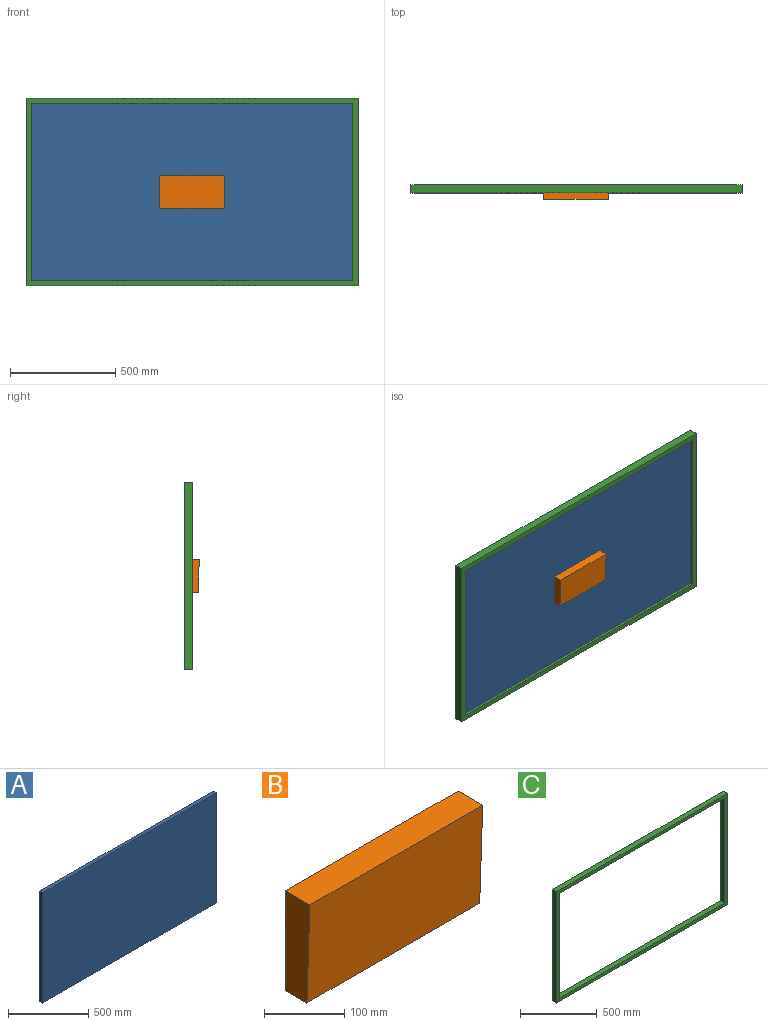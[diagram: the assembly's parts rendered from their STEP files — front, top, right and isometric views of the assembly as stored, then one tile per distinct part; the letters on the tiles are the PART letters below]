
ASSEMBLY  parts=3 mates=2
PART A: 6 faces, bbox 1524x25.4x838.2 mm
  f0: plane 1524x25.4mm, normal (0,0,1), area 38709.6mm2, adj f1,f3,f4,f5
  f1: plane 838.2x25.4mm, normal (-1,0,0), area 21290.3mm2, adj f0,f2,f4,f5
  f2: plane 1524x25.4mm, normal (0,0,-1), area 38709.6mm2, adj f1,f3,f4,f5
  f3: plane 838.2x25.4mm, normal (1,0,0), area 21290.3mm2, adj f0,f2,f4,f5
  f4: plane 1524x838.2mm, normal (0,-1,0), area 1277416.8mm2, adj f0,f1,f2,f3
  f5: plane 1524x838.2mm, normal (0,1,0), area 1277416.8mm2, adj f0,f1,f2,f3
PART B: 6 faces, bbox 304.8x43.4x152.4 mm
  f0: plane 304.8x152.4mm, normal (0,1,0), area 46451.5mm2, adj f1,f3,f4,f5
  f1: plane 304.8x43.42mm, normal (0,0,1), area 13235mm2, adj f0,f2,f4,f5
  f2: plane 304.8x152.4mm, normal (0,-1,-0.03), area 46479.8mm2, adj f1,f3,f4,f5
  f3: plane 304.8x38.1mm, normal (0,0,-1), area 11612.9mm2, adj f0,f2,f4,f5
  f4: plane 152.4x43.42mm, normal (1,0,0), area 6212mm2, adj f0,f1,f2,f3
  f5: plane 152.4x43.42mm, normal (-1,0,0), area 6212mm2, adj f0,f1,f2,f3
PART C: 10 faces, bbox 1574.8x38.1x889 mm
  f0: plane 1574.8x38.1mm, normal (0,0,1), area 59999.9mm2, adj f1,f7,f8,f9
  f1: plane 889x38.1mm, normal (-1,0,0), area 33870.9mm2, adj f0,f2,f8,f9
  f2: plane 1574.8x38.1mm, normal (0,0,-1), area 59999.9mm2, adj f1,f7,f8,f9
  f3: plane 838.2x38.1mm, normal (1,0,0), area 31935.4mm2, adj f4,f6,f8,f9
  f4: plane 1524x38.1mm, normal (0,0,-1), area 58064.4mm2, adj f3,f5,f8,f9
  f5: plane 838.2x38.1mm, normal (-1,0,0), area 31935.4mm2, adj f4,f6,f8,f9
  f6: plane 1524x38.1mm, normal (0,0,1), area 58064.4mm2, adj f3,f5,f8,f9
  f7: plane 889x38.1mm, normal (1,0,0), area 33870.9mm2, adj f0,f2,f8,f9
  f8: plane 1574.8x889mm, normal (0,-1,0), area 122580.4mm2, adj f0,f1,f2,f3,f4,f5,f6,f7
  f9: plane 1574.8x889mm, normal (0,1,0), area 122580.4mm2, adj f0,f1,f2,f3,f4,f5,f6,f7
PLACE A t=(-299.74,-81.63,34.95)mm
PLACE B t=(-364.06,-81.93,-6.1)mm
PLACE C t=(158.2,-81.63,-140.34)mm
MATE fastened A.f0 <-> C.f4  axis (0,0,1) through (550.34,-81.63,451.38)mm
MATE fastened B.f0 <-> A.f4  axis (0,1,0) through (-211.66,-107.03,32.28)mm
